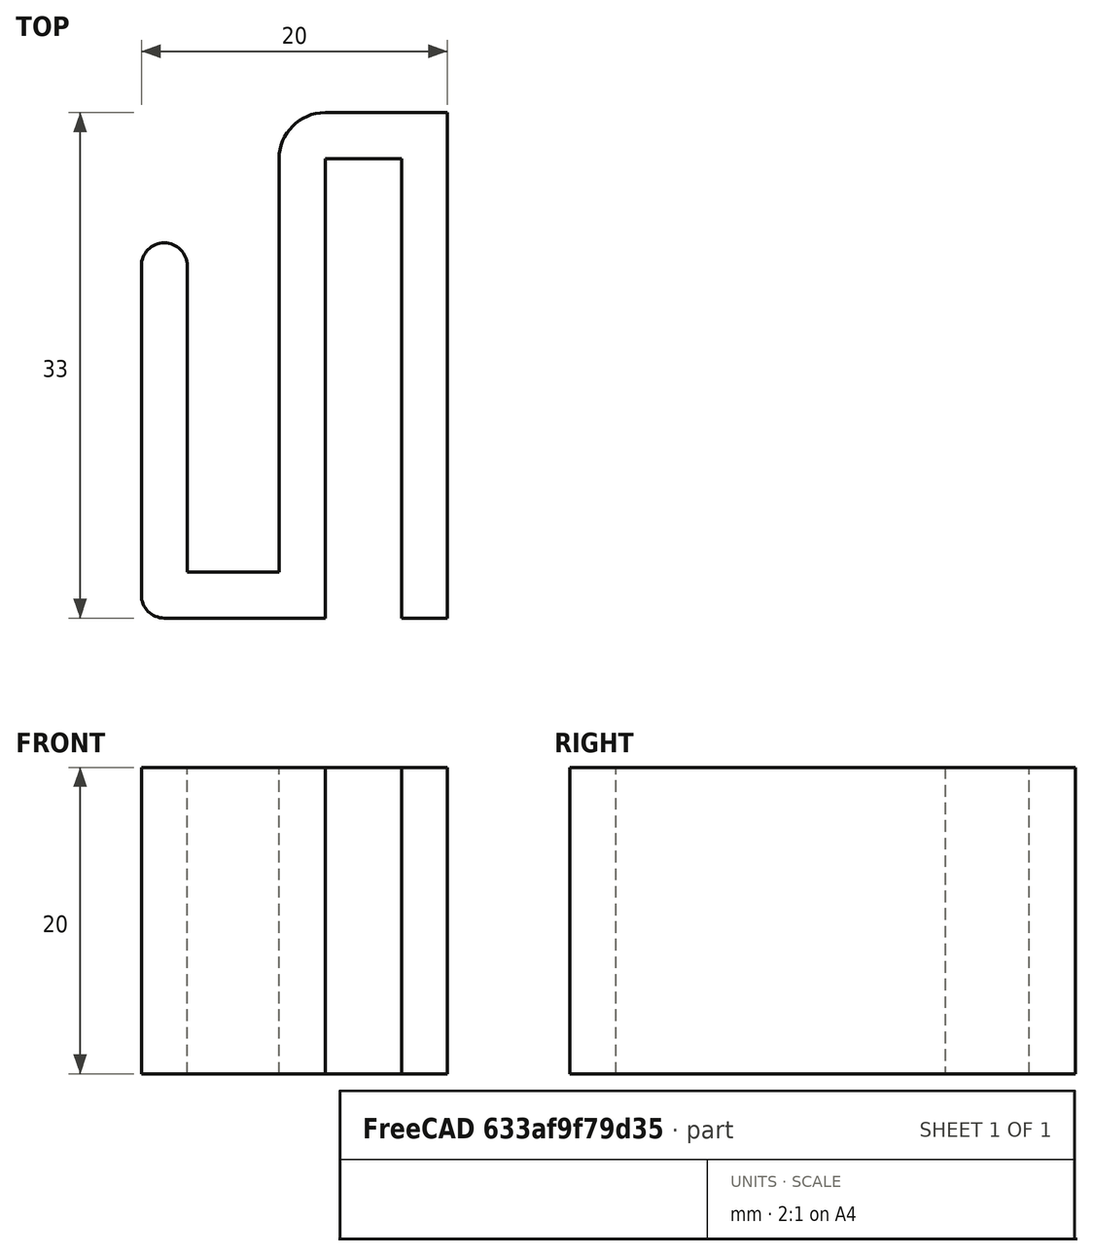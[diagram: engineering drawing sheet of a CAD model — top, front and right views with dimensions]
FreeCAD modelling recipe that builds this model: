
FCSTD DOCUMENT  (FreeCAD 2022.111R30764 (Git))
Label: garage shelf hook
License: All rights reserved
LicenseURL: http://en.wikipedia.org/wiki/All_rights_reserved
objects: Sketcher::SketchObject×1, PartDesign::Pad×1, PartDesign::Body×1
note: 5 computed .brp shape members not serialized (recipe doc carries the construction recipe); baked Part::Feature solids carry a one-line shape summary decoded from their .brp

FEATURE [Sketcher::SketchObject] Sketch
  FullyConstrained = true
  MapMode = 5
  Support = -> [XY_Plane]
  TreeRank = 11
  sketch-geometry (15):
    g0: LineSegment StartX=0 StartY=0 StartZ=0 EndX=0 EndY=30 EndZ=0
    g1: LineSegment StartX=0 StartY=30 StartZ=0 EndX=-5 EndY=30 EndZ=0
    g2: LineSegment StartX=-5 StartY=30 StartZ=0 EndX=-5 EndY=0 EndZ=0
    g3: LineSegment StartX=0 StartY=0 StartZ=0 EndX=3 EndY=0 EndZ=0
    g4: LineSegment StartX=3 StartY=0 StartZ=0 EndX=3 EndY=33 EndZ=0
    g5: LineSegment StartX=3 StartY=33 StartZ=0 EndX=-5 EndY=33 EndZ=0
    g6: LineSegment StartX=-8 StartY=30 StartZ=0 EndX=-8 EndY=3 EndZ=0
    g7: LineSegment StartX=-8 StartY=3 StartZ=0 EndX=-14 EndY=3 EndZ=0
    g8: LineSegment StartX=-14 StartY=3 StartZ=0 EndX=-14 EndY=23 EndZ=0
    g9: LineSegment StartX=-15.5 StartY=0 StartZ=0 EndX=-5 EndY=0 EndZ=0
    g10: ArcOfCircle CenterX=-15.5 CenterY=23 CenterZ=0 NormalX=0 NormalY=0 NormalZ=1 AngleXU=0 Radius=1.5 StartAngle=7e-16 EndAngle=3.14159
    g11: LineSegment StartX=-17 StartY=1.5 StartZ=0 EndX=-17 EndY=23 EndZ=0
    g12: ArcOfCircle CenterX=-15.5 CenterY=1.5 CenterZ=0 NormalX=0 NormalY=0 NormalZ=1 AngleXU=0 Radius=1.5 StartAngle=3.14159 EndAngle=4.71239
    g13: ArcOfCircle CenterX=-5 CenterY=30 CenterZ=0 NormalX=0 NormalY=0 NormalZ=1 AngleXU=0 Radius=3 StartAngle=1.5708 EndAngle=3.14159
    g14: GeomPoint [constr] X=-8 Y=33 Z=0
  constraints (41):
    c: Coincident(g-1,g0)
    c: PointOnObject(g0,g-2)
    c: Coincident(g0,g1)
    c: Horizontal(g1)
    c: Coincident(g1,g2)
    c: PointOnObject(g2,g-1)
    c: Vertical(g2)
    c: Coincident(g0,g3)
    c: PointOnObject(g3,g-1)
    c: Coincident(g3,g4)
    c: Vertical(g4)
    c: Coincident(g4,g5)
    c: Horizontal(g5)
    c: Vertical(g6)
    c: Coincident(g6,g7)
    c: Horizontal(g7)
    c: Vertical(g8)
    c: Coincident(g9,g2)
    c: DistanceX(g1,g1) = 5
    c: DistanceY(g0,g0) = 30
    c: DistanceX(g3,g3) = 3
    c: DistanceX(g14,g1) = 3
    c: DistanceY(g1,g14) = 3
    c: DistanceY(g2,g6) = 3
    c: Horizontal(g9)
    c: DistanceX(g10,g8) = 3
    c: Horizontal(g10,g8)
    c: Tangent(g10,g8) = -1.5708
    c: Coincident(g11,g10)
    c: Vertical(g11)
    c: Tangent(g11,g12) = 1.5708
    c: Tangent(g9,g12) = -1.5708
    c: Diameter(g12) = 3
    c: DistanceX(g8,g6) = 6
    c: DistanceY(g8,g8) = 20
    c: Coincident(g7,g8)
    c: PointOnObject(g14,g5)
    c: PointOnObject(g14,g6)
    c: Tangent(g5,g13) = -1.5708
    c: Tangent(g6,g13) = -1.5708
    c: Radius(g13) = 3
FEATURE [PartDesign::Pad] Pad
  AddSubType = 0
  AlongSketchNormal = false
  CheckUpToFaceLimits = true
  ClaimChildren = false
  Direction = (0,0,1)
  Fit = 0
  FitJoin = 0
  InnerFit = 0
  InnerFitJoin = 0
  InnerTaperAngle = 0
  InnerTaperAngleRev = 0
  Length = 20
  Length2 = 100
  Linearize = true
  NewSolid = false
  Profile = -> Sketch
  Suppress = false
  TreeRank = 12
  Type = 0
  _ProfileBasedVersion = 1
FEATURE [PartDesign::Body] Body
  AutoGroupSolids = false
  ExportMode = 0
  Group = -> [Sketch,Pad]
  Origin = -> Origin
  Tip = -> Pad
  TreeRank = 10
  _ExportChildren = -> [Pad]
  _GroupVersion = 1
